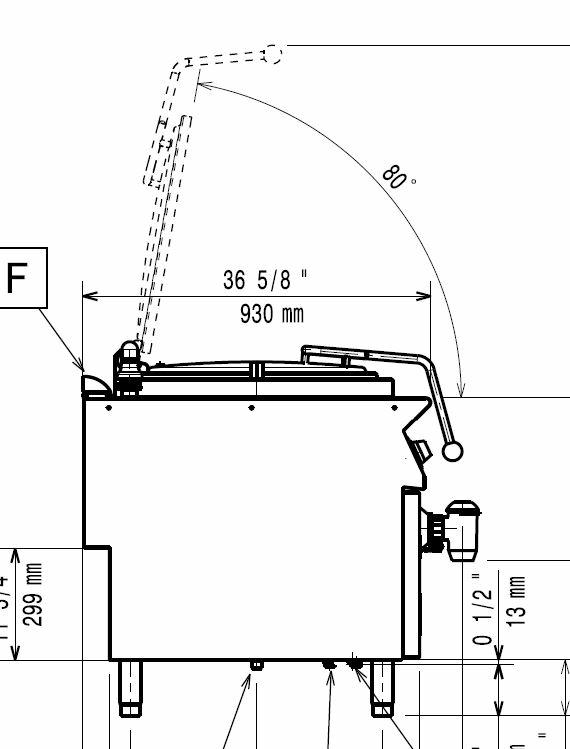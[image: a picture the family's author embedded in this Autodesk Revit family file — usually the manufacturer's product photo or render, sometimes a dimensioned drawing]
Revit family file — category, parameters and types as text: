
# Revit family: QF_ELECTROLUXPROFESSIONAL_391103_E9BSGHIRFR
name_source: partatom
category: Specialty Equipment
revit_build: Autodesk Revit 2018 (Build: 20190510_1515(x64)
units: mm (PartAtom-declared; Revit-internal decimal feet)

## family parameters
Always vertical = Yes
Cut with Voids When Loaded = No
Part Type = Normal
Room Calculation Point = No
Round Connector Dimension = Use Diameter
Shared = No
Work Plane-Based = No

## types (1)
- QF_ELECTROLUXPROFESSIONAL_391103_E9BSGHIRFR
    Apparent Power = 0 VA
    Cold Water Connection Height = 0 mm  [stored 0 ft]
    Cold Water Maximum Pressure = 0.00 psi
    Cold Water Minimum Pressure = 0.00 psi
    Cold Water Size = 1"
    Conn Conduit = Yes
    Depth = 930 mm
    Description = 900XP GAS CYLINDRICAL BOILING PAN 150LT INDIRECT HEAT WITH AUTOMATIC REFILL- 230 V
    Direct Waste Size = 2"
    FL Amps = 0 A
    Gas Connection Height = 0 mm  [stored 0 ft]
    Gas Input = 81816.0 Btu/h
    Gas KW = 24
    Gas Size = 1"
    HP = 0.1 HP
    Height = 850 mm  [stored 2.78871 ft]
    Hot Water Connection Height = 0 mm  [stored 0 ft]
    Hot Water Consumption = 0 GPM
    Hot Water Maximum Pressure = 0.00 psi
    Hot Water Minimum Pressure = 0.00 psi
    Hot Water Size = 1"
    Indirect Waste Connection Height = 0 mm  [stored 0 ft]
    Indirect Waste Size = 1"
    Manufacturer = ELECTROLUX
    Max Overcurrent Protection = 0 A
    Min Ckt Ampacity = 0 A
    Model = 391103
    Phase = 1
    URL = www.electrolux.com
    URL Cutsheet = www.electrolux.com
    Volts = 230 V
    Watts = 0 W
    Weight in Pounds = 135
    Width = 800 mm  [stored 2.62467 ft]

note: [stored X ft] marks values corroborated as IEEE doubles in the binary element streams (Revit-internal decimal feet)

## geometry (parser evidence)
native form markers: Blend x18, Sweep x2
no freeform markers — native parametric forms only
